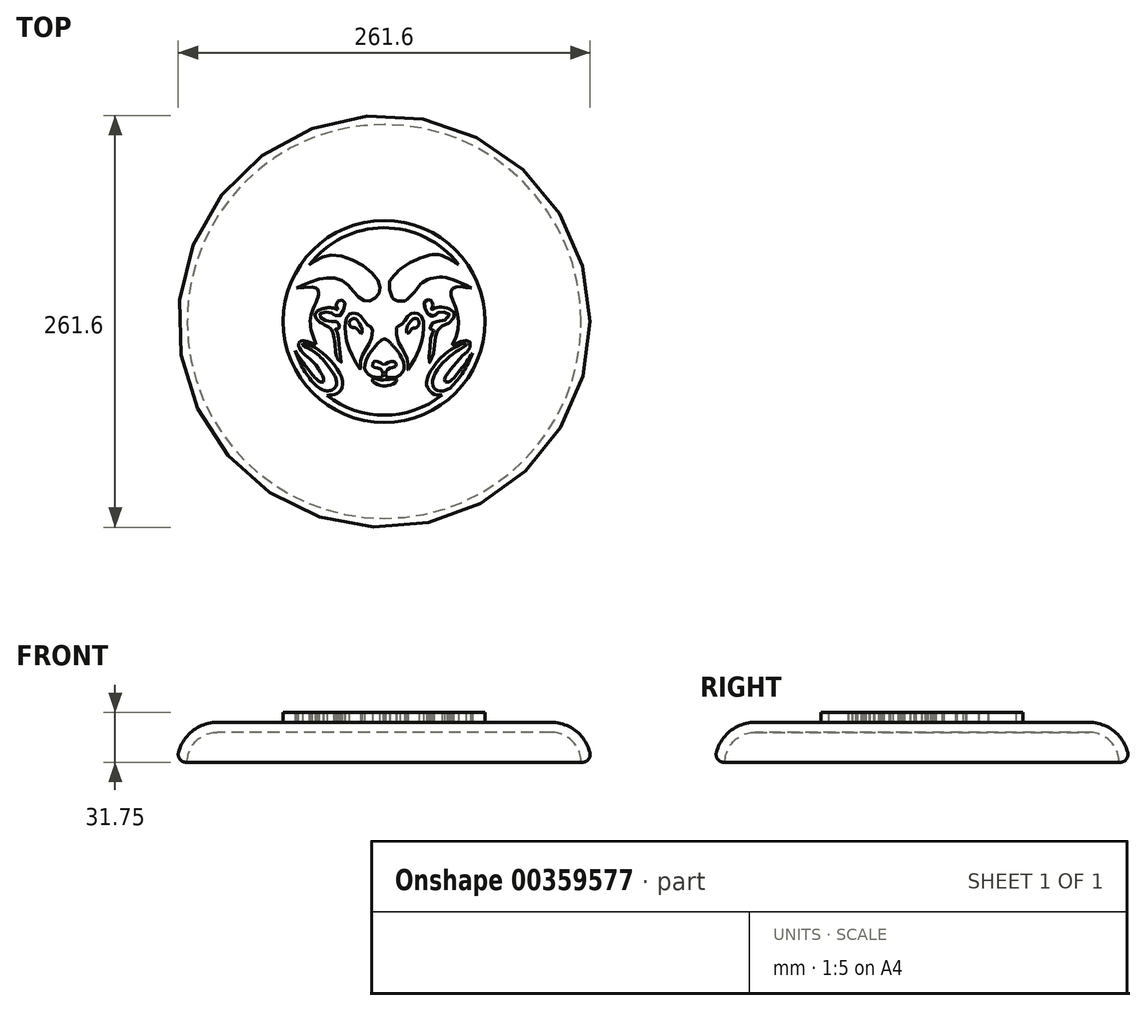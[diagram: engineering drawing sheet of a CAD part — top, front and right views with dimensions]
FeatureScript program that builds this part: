
annotation { "Feature Type Name" : "Feature", "Feature Type Description" : "" }
export const myFeature = defineFeature(function(context is Context, id is Id, definition is map)
    precondition{}
    {
        {
            var Q0;
            Q0=qCreatedBy(makeId("Top.planeOp"),FACE);
            var sketch = newSketch(context, id + "F0", { "sketchPlane" : qUnion([Q0])});
            skCircle(sketch, "E0", {"center": v(0, 0) * mm, "radius": 131.44 * mm});
            skSolve(sketch);
        }
        {
            var Q0;
            Q0=makeQuery(id+"F0.imprint","IMPRINT",FACE,{"disambiguationData":[TD([[makeQuery(id+"F0.imprint","IMPRINT",EDGE,{"derivedFrom":sQuery(id+"F0.wireOp",EDGE,"E0")}),1.0]])]});
            extrude(context, id + "F1", {"entities" : qUnion([Q0]), "depth" : 25.4 * mm});
        }
        {
            var Q0;
            Q0=makeQuery(id+"F1.opExtrude","CAP_EDGE",EDGE,{"disambiguationData":[OSD([sQuery(id+"F0.wireOp",EDGE,"E0")])],"isStart":false});
            fillet(context, id + "F2", {"entities" : qUnion([Q0]), "radius" : 25.4 * mm, "tangentPropagation" : true, "allowEdgeOverflow" : false});
        }
        {
            var Q0;
            {var subQ0=sQuery(id+"F0.wireOp",EDGE,"E0");Q0=makeQuery(id+"F2.opFillet","BLEND_EDGE",EDGE,{"blendedFrom":[makeQuery(id+"F1.opExtrude","CAP_EDGE",EDGE,{"disambiguationData":[OSD([subQ0])],"isStart":false}),makeQuery(id+"F1.opExtrude","CAP_FACE",FACE,{"disambiguationData":[OSD([subQ0])],"isStart":true})],"blendedInto":[makeQuery(id+"F1.opExtrude","CAP_FACE",FACE,{"disambiguationData":[OSD([subQ0])],"isStart":true})]});}
            fillet(context, id + "F3", {"entities" : qUnion([Q0]), "radius" : 5.08 * mm, "tangentPropagation" : true, "allowEdgeOverflow" : false});
        }
        {
            var Q0;
            Q0=makeQuery(id+"F1.opExtrude","CAP_FACE",FACE,{"disambiguationData":[OSD([sQuery(id+"F0.wireOp",EDGE,"E0")])],"isStart":true});
            shell(context, id + "F4", {"entities" : qUnion([Q0]), "thickness" : 6.35 * mm});
        }
        {
            var Q0;
            Q0=makeQuery(id+"F1.opExtrude","CAP_FACE",FACE,{"disambiguationData":[OSD([sQuery(id+"F0.wireOp",EDGE,"E0")])],"isStart":false});
            var sketch = newSketch(context, id + "F5", { "sketchPlane" : qUnion([Q0])});
            skCircle(sketch, "E1", {"center": v(0, 0) * mm, "radius": 67.22 * mm});
            skCircle(sketch, "E2", {"center": v(0, 0) * mm, "radius": 64.1 * mm});
            skCircle(sketch, "E3", {"center": v(0, 0) * mm, "radius": 59.52 * mm});
            skFitSpline(sketch, "E4", {"points": [v(-47.61, 35.71) * mm, v(-30.33, 42.03) * mm, v(-3.45, 25.44) * mm, v(-5.16, 15.48) * mm, v(-13.42, 13.42) * mm, v(-24.24, 24.18) * mm, v(-39.23, 27.35) * mm, v(-55.63, 21.17) * mm], "startDerivative": vector(77.27, 62.1) * mm, "endDerivative": vector(-80.83, -38.7) * mm});
            skFitSpline(sketch, "E5", {"points": [v(3.63, 26.05) * mm, v(11.7, 34.34) * mm, v(24.03, 40.71) * mm, v(34.24, 42.41) * mm, v(47.28, 36.15) * mm], "startDerivative": vector(32.1, 37.54) * mm, "endDerivative": vector(50.12, -31.58) * mm});
            skFitSpline(sketch, "E6", {"points": [v(3.63, 26.05) * mm, v(5.75, 14.57) * mm, v(13.4, 12.87) * mm], "startDerivative": vector(-3.44, -18.37) * mm, "endDerivative": vector(17, 0) * mm});
            skFitSpline(sketch, "E7", {"points": [v(13.4, 12.87) * mm, v(19.78, 19.46) * mm, v(23.18, 23.7) * mm, v(29.77, 27.32) * mm, v(38.28, 27.96) * mm, v(55.55, 21.36) * mm], "startDerivative": vector(36.21, 34.6) * mm, "endDerivative": vector(89.25, -41.03) * mm});
            skFitSpline(sketch, "E8", {"points": [v(-45.68, 22) * mm, v(-55.63, 21.17) * mm], "startDerivative": vector(-9.94, -0.84) * mm, "endDerivative": vector(-9.94, -0.84) * mm});
            skFitSpline(sketch, "E9", {"points": [v(-43.13, -14.76) * mm, v(-46.53, -4.56) * mm, v(-46.1, 5.43) * mm, v(-41.86, 16.06) * mm, v(-42.28, 20.3) * mm, v(-45.68, 22) * mm], "startDerivative": vector(-17.3, 43.12) * mm, "endDerivative": vector(-28.36, 8.66) * mm});
            skFitSpline(sketch, "E10", {"points": [v(-43.13, -14.76) * mm, v(-49.94, -12.43) * mm, v(-52.91, -12.43) * mm, v(-54.4, -14.76) * mm, v(-52.06, -19.44) * mm, v(-45.68, -25.18) * mm, v(-38.67, -35.6) * mm, v(-38.46, -38.36) * mm], "startDerivative": vector(-45.49, 17.24) * mm, "endDerivative": vector(-2.99, -22.74) * mm});
            skFitSpline(sketch, "E11", {"points": [v(-38.46, -38.36) * mm, v(-40.58, -38.36) * mm, v(-56.56, -18.53) * mm], "startDerivative": vector(-8.24, -2.87) * mm, "endDerivative": vector(-31.36, 47.89) * mm});
            skFitSpline(sketch, "E12", {"points": [v(-51.85, -14.13) * mm, v(-49.94, -14.34) * mm, v(-40.58, -18.8) * mm, v(-27.4, -34.53) * mm, v(-27.2, -43.03) * mm, v(-31.44, -46.22) * mm, v(-36.4, -47.09) * mm], "startDerivative": vector(19.14, -0.5) * mm, "endDerivative": vector(-34.7, -8.03) * mm});
            skFitSpline(sketch, "E13", {"points": [v(-51.85, -14.13) * mm, v(-51.85, -15.01) * mm, v(-48.61, -16.9) * mm, v(-39.08, -24) * mm, v(-32.25, -33) * mm], "startDerivative": vector(-2, -8.15) * mm, "endDerivative": vector(8.92, -10.28) * mm});
            skFitSpline(sketch, "E14", {"points": [v(-32.25, -33) * mm, v(-31.02, -35.52) * mm, v(-30.42, -37.85) * mm, v(-30.43, -40.22) * mm, v(-31.46, -42.3) * mm, v(-33.64, -43.63) * mm, v(-36, -44.03) * mm, v(-38.43, -43.74) * mm, v(-43.04, -41.1) * mm], "startDerivative": vector(10.86, -20.07) * mm, "endDerivative": vector(-28.3, 19.1) * mm});
            skFitSpline(sketch, "E15", {"points": [v(-29.55, 7.8) * mm, v(-30.23, 9.26) * mm, v(-30.4, 11.4) * mm, v(-29.55, 12.85) * mm, v(-28.18, 13.54) * mm, v(-26.64, 13.46) * mm, v(-25.27, 12.7) * mm, v(-24.84, 10.64) * mm, v(-26.64, 5.58) * mm, v(-28.27, 3.53) * mm, v(-30.75, 3.6) * mm, v(-32.25, 4.63) * mm, v(-33.64, 5.48) * mm, v(-36.57, 5.99) * mm, v(-40.33, 5.3) * mm, v(-40.85, 4.44) * mm, v(-40.76, 3.07) * mm, v(-38.7, 1.36) * mm, v(-35.63, 0) * mm, v(-32.25, 0) * mm, v(-30.58, 0) * mm, v(-29.13, -1.36) * mm, v(-28.36, -2.38) * mm, v(-28.27, -3.92) * mm, v(-29.56, -4.53) * mm, v(-30.58, -4.53) * mm, v(-31.01, -4.96) * mm, v(-30.41, -6.15) * mm, v(-29.3, -8.46) * mm, v(-28.88, -11.63) * mm, v(-28.8, -14.71) * mm, v(-27.68, -21.81) * mm, v(-27.52, -26.18) * mm, v(-29.23, -24.13) * mm], "startDerivative": vector(-29.16, 51.27) * mm, "endDerivative": vector(-36.35, 67.29) * mm});
            skFitSpline(sketch, "E16", {"points": [v(-29.23, -24.13) * mm, v(-30.17, -22.25) * mm, v(-30.93, -18.48) * mm, v(-31.44, -12.66) * mm, v(-32.47, -7.7) * mm, v(-33.66, -4.88) * mm, v(-35.46, -3.43) * mm, v(-38.97, -1.55) * mm, v(-42.73, 1.35) * mm, v(-43.93, 3.92) * mm], "startDerivative": vector(-11.7, 19.95) * mm, "endDerivative": vector(-4.1, 19.55) * mm});
            skFitSpline(sketch, "E17", {"points": [v(-43.93, 3.92) * mm, v(-43.73, 4.9) * mm, v(-42.95, 6.2) * mm, v(-41.25, 7.23) * mm, v(-38.61, 8.17) * mm, v(-36.68, 8.64) * mm, v(-33.58, 8.75) * mm, v(-30.87, 7.92) * mm, v(-29.8, 7.41) * mm, v(-29.55, 7.8) * mm], "startDerivative": vector(1.43, 11.35) * mm, "endDerivative": vector(3.04, 9.31) * mm});
            skFitSpline(sketch, "E18", {"points": [v(-19.48, 5.43) * mm, v(-22.36, 4.44) * mm, v(-24.06, 1.7) * mm, v(-24.65, -0.96) * mm, v(-24.8, -6.22) * mm, v(-22.96, -15.3) * mm, v(-19.2, -23.73) * mm, v(-14.92, -30.38) * mm, v(-14.99, -28.3) * mm, v(-14.25, -22.54) * mm, v(-10.77, -16.24) * mm, v(-8.33, -11.28) * mm, v(-7.58, -4.1) * mm, v(-8.91, -3.37) * mm, v(-12.02, -0.71) * mm, v(-14.38, 2.68) * mm, v(-16.08, 4.44) * mm, v(-19.48, 5.43) * mm]});
            skFitSpline(sketch, "E19", {"points": [v(-14.75, -7.52) * mm, v(-14.16, -7.3) * mm, v(-14.38, -4.2) * mm, v(-16.52, 0) * mm, v(-18.22, 1.56) * mm, v(-20, 1.7) * mm, v(-21.18, 1.04) * mm, v(-22, 0) * mm, v(-21.85, -2.59) * mm, v(-20.07, -3.84) * mm, v(-18.6, -3.9) * mm, v(-16.9, -4.8) * mm, v(-14.75, -7.52) * mm]});
            skFitSpline(sketch, "E20", {"points": [v(7.72, -3.92) * mm, v(8.6, -3.33) * mm, v(10, -2.59) * mm, v(12.08, -0.96) * mm, v(14.15, 2.16) * mm, v(16.15, 4.44) * mm, v(18.14, 5.43) * mm, v(19.77, 5.43) * mm, v(22.58, 4.44) * mm, v(24.5, 1.44) * mm, v(25.08, -3.51) * mm, v(24.2, -11.43) * mm, v(21.16, -20.16) * mm, v(15.24, -30.53) * mm, v(15.1, -30.68) * mm, v(15.1, -27.72) * mm, v(14.13, -22.62) * mm, v(11.4, -17.08) * mm, v(8.75, -12.28) * mm, v(7.72, -3.92) * mm]});
            skFitSpline(sketch, "E21", {"points": [v(14.51, -7.3) * mm, v(14.3, -5.83) * mm, v(14.66, -3.02) * mm, v(16.59, 0) * mm, v(18.36, 1.5) * mm, v(19.62, 1.87) * mm, v(20.8, 1.8) * mm, v(21.98, 0) * mm, v(21.98, -2.41) * mm, v(19.98, -4.04) * mm, v(18.58, -4.12) * mm, v(16.8, -5.45) * mm, v(15.7, -7.3) * mm, v(14.51, -7.3) * mm]});
            skFitSpline(sketch, "E22", {"points": [v(0, -11.29) * mm, v(-1.32, -11.66) * mm, v(-6.18, -16.4) * mm, v(-10.78, -22.9) * mm, v(-12.53, -28.75) * mm, v(-11.9, -31.23) * mm, v(-9.92, -33.6) * mm, v(-6.93, -35.2) * mm, v(-1.33, -35.2) * mm, v(-0.59, -33.44) * mm, v(-1.02, -31.72) * mm, v(-2.43, -30.37) * mm, v(-4.18, -29.58) * mm, v(-6.33, -29.15) * mm, v(-7.25, -28.58) * mm, v(-7.3, -26.82) * mm, v(-6.46, -25.41) * mm, v(-4.93, -25.2) * mm, v(-2.47, -25.98) * mm, v(0, -27.64) * mm], "startDerivative": vector(-31.8, -2.62) * mm, "endDerivative": vector(44.21, -33.7) * mm});
            skFitSpline(sketch, "E23", {"points": [v(0, -27.64) * mm, v(0.87, -27.03) * mm, v(2.45, -26.05) * mm, v(5.3, -25.39) * mm, v(6.8, -25.6) * mm, v(7.54, -27.03) * mm, v(7.5, -28.28) * mm, v(5.38, -29.25) * mm, v(3.5, -29.7) * mm, v(1.56, -31.24) * mm, v(0.95, -33.08) * mm, v(1.08, -34.75) * mm, v(2.92, -35.5) * mm, v(7.44, -35.22) * mm, v(11.48, -32.66) * mm, v(12.76, -29.15) * mm, v(12.01, -25.37) * mm, v(10, -21.16) * mm, v(10, -21.3) * mm], "startDerivative": vector(21.67, 14.87) * mm, "endDerivative": vector(2.26, -14.92) * mm});
            skFitSpline(sketch, "E24", {"points": [v(10, -21.16) * mm, v(7.98, -18.18) * mm, v(4.89, -14.7) * mm, v(2.57, -12.26) * mm, v(0, -11.29) * mm], "startDerivative": vector(-7.23, 11.72) * mm, "endDerivative": vector(-17.66, -0.8) * mm});
            skFitSpline(sketch, "E25", {"points": [v(-6.79, -36.27) * mm, v(-3.38, -36.84) * mm, v(0, -37.08) * mm, v(4.64, -36.65) * mm, v(7.17, -36.5) * mm, v(7.9, -36.77) * mm, v(7.22, -38.66) * mm, v(3.23, -40.45) * mm, v(0.5, -40.93) * mm, v(-3.38, -40.26) * mm, v(-6.63, -38.74) * mm, v(-7.31, -37.9) * mm, v(-7.36, -36.85) * mm, v(-6.79, -36.27) * mm]});
            skFitSpline(sketch, "E26", {"points": [v(55.55, 21.36) * mm, v(51.55, 21.66) * mm, v(48.5, 22.07) * mm, v(45.1, 21.86) * mm, v(43.46, 20.87) * mm, v(42.63, 19.97) * mm, v(42.27, 18.36) * mm, v(42.6, 15.67) * mm, v(44.35, 11.35) * mm, v(46.54, 4.83) * mm, v(47.07, -2.33) * mm, v(45.4, -10.18) * mm, v(43.14, -15.31) * mm, v(46.3, -13.8) * mm, v(51.13, -12.13) * mm, v(54, -12.5) * mm, v(54.9, -15.06) * mm, v(52.88, -19.1) * mm, v(50.62, -20.95) * mm, v(43.1, -29.12) * mm, v(39.85, -33.64) * mm], "startDerivative": vector(-84.35, 4.69) * mm, "endDerivative": vector(-30.59, -53.96) * mm});
            skFitSpline(sketch, "E27", {"points": [v(39.85, -33.64) * mm, v(38.77, -35.63) * mm, v(38.67, -38.25) * mm, v(41.39, -38.16) * mm, v(46.09, -33.64) * mm, v(51.06, -27.2) * mm, v(56.04, -20.04) * mm], "startDerivative": vector(-10.25, -15.17) * mm, "endDerivative": vector(21.92, 32.35) * mm});
            skFitSpline(sketch, "E28", {"points": [v(52.03, -14.06) * mm, v(51.3, -13.85) * mm, v(46.08, -15.9) * mm, v(41.17, -18.63) * mm, v(33.17, -26.27) * mm, v(27.84, -34.54) * mm, v(27.08, -37.4) * mm, v(26.93, -39.63) * mm, v(28.02, -42.86) * mm, v(31.5, -45.99) * mm, v(34.03, -46.78) * mm, v(36.82, -46.76) * mm], "startDerivative": vector(-14.14, 9.02) * mm, "endDerivative": vector(38.58, 2.68) * mm});
            skFitSpline(sketch, "E29", {"points": [v(52.03, -14.06) * mm, v(52.33, -14.5) * mm, v(51.77, -15.32) * mm, v(48, -17.66) * mm, v(44.02, -20.3) * mm, v(39.01, -24.61) * mm, v(33.93, -30.48) * mm, v(30.95, -36.6) * mm, v(30.75, -39.3) * mm, v(31.5, -41.59) * mm, v(32.33, -42.86) * mm, v(33.85, -43.92) * mm, v(37.33, -44.24) * mm, v(42.03, -42.14) * mm], "startDerivative": vector(14.03, -13.8) * mm, "endDerivative": vector(49.7, 28.64) * mm});
            skFitSpline(sketch, "E30", {"points": [v(28.02, 13.77) * mm, v(29.3, 13.5) * mm, v(30.47, 12.34) * mm, v(30.81, 11.02) * mm, v(30.85, 9.5) * mm, v(30.2, 8.53) * mm, v(29.98, 7.84) * mm, v(30.45, 7.7) * mm, v(32.15, 8.42) * mm, v(34.93, 9) * mm, v(38.75, 8.7) * mm, v(42.54, 7.19) * mm, v(44.16, 5.64) * mm, v(44.45, 4.16) * mm, v(44.05, 2.1) * mm], "startDerivative": vector(21.18, -1.44) * mm, "endDerivative": vector(-6.98, -27.5) * mm});
            skFitSpline(sketch, "E31", {"points": [v(44.05, 2.1) * mm, v(43.08, 0.92) * mm, v(40.68, -1.15) * mm, v(37.43, -2.68) * mm, v(35.72, -3.56) * mm, v(34.51, -4.73) * mm, v(33.21, -7.56) * mm, v(32.79, -9.04) * mm, v(32.45, -10.35) * mm, v(31.9, -15.86) * mm, v(31.64, -19.16) * mm, v(29.7, -24.74) * mm, v(28.45, -26.26) * mm, v(28.32, -22.67) * mm, v(28.9, -20.57) * mm, v(29.3, -15.27) * mm, v(29.46, -10.55) * mm, v(30.65, -6.7) * mm, v(31.82, -4.8) * mm, v(29.39, -4.75) * mm, v(28.9, -2.99) * mm, v(30.43, -1.02) * mm, v(31.24, -0.43) * mm, v(32.34, 0) * mm, v(35.75, 0.19) * mm, v(38.93, 1.16) * mm, v(41.39, 3.39) * mm, v(41.25, 4.76) * mm, v(39.8, 5.54) * mm, v(37.48, 5.94) * mm, v(35.48, 5.95) * mm, v(34.04, 5.42) * mm, v(32.17, 3.88) * mm, v(30.83, 3.32) * mm, v(28.65, 3.9) * mm, v(27.04, 6) * mm, v(26.26, 7.6) * mm, v(25.69, 9.27) * mm, v(25.43, 10.94) * mm, v(25.69, 12.42) * mm, v(26.52, 13.31) * mm, v(28.02, 13.77) * mm], "startDerivative": vector(-43.21, -56.66) * mm, "endDerivative": vector(81.46, 17.12) * mm});
            skSolve(sketch);
        }
        {
            var Q0;
            {var subQ0=sQuery(id+"F5.wireOp",EDGE,"E4");Q0=makeQuery(id+"F5.imprint","IMPRINT",FACE,{"disambiguationData":[TD([[makeQuery(id+"F5.imprint","IMPRINT",EDGE,{"derivedFrom":subQ0}),-1.0]])]});}
            var Q1;
            {var subQ0=sQuery(id+"F5.wireOp",EDGE,"E5");Q1=makeQuery(id+"F5.imprint","IMPRINT",FACE,{"disambiguationData":[TD([[makeQuery(id+"F5.imprint","IMPRINT",EDGE,{"derivedFrom":subQ0}),-1.0]])]});}
            var Q2;
            Q2=makeQuery(id+"F5.imprint","IMPRINT",FACE,{"disambiguationData":[TD([[makeQuery(id+"F5.imprint","IMPRINT",EDGE,{"derivedFrom":sQuery(id+"F5.wireOp",EDGE,"E30")}),-1.0]])]});
            var Q3;
            Q3=makeQuery(id+"F5.imprint","IMPRINT",FACE,{"disambiguationData":[TD([[makeQuery(id+"F5.imprint","IMPRINT",EDGE,{"derivedFrom":sQuery(id+"F5.wireOp",EDGE,"E20")}),-1.0]])]});
            var Q4;
            Q4=makeQuery(id+"F5.imprint","IMPRINT",FACE,{"disambiguationData":[TD([[makeQuery(id+"F5.imprint","IMPRINT",EDGE,{"derivedFrom":sQuery(id+"F5.wireOp",EDGE,"E18")}),1.0]])]});
            var Q5;
            {var subQ0=sQuery(id+"F5.wireOp",EDGE,"E22");Q5=makeQuery(id+"F5.imprint","IMPRINT",FACE,{"disambiguationData":[TD([[makeQuery(id+"F5.imprint","IMPRINT",EDGE,{"derivedFrom":subQ0}),1.0]])]});}
            var Q6;
            Q6=makeQuery(id+"F5.imprint","IMPRINT",FACE,{"disambiguationData":[TD([[makeQuery(id+"F5.imprint","IMPRINT",EDGE,{"derivedFrom":sQuery(id+"F5.wireOp",EDGE,"E25")}),-1.0]])]});
            var Q7;
            {var subQ0=sQuery(id+"F5.wireOp",EDGE,"E28");Q7=makeQuery(id+"F5.imprint","IMPRINT",FACE,{"disambiguationData":[TD([[makeQuery(id+"F5.imprint","IMPRINT",EDGE,{"derivedFrom":subQ0}),1.0]])]});}
            var Q8;
            {var subQ0=sQuery(id+"F5.wireOp",EDGE,"E26");Q8=makeQuery(id+"F5.imprint","IMPRINT",FACE,{"disambiguationData":[TD([[makeQuery(id+"F5.imprint","IMPRINT",EDGE,{"derivedFrom":subQ0}),1.0]])]});}
            var Q9;
            {var subQ0=sQuery(id+"F5.wireOp",EDGE,"E8");Q9=makeQuery(id+"F5.imprint","IMPRINT",FACE,{"disambiguationData":[TD([[makeQuery(id+"F5.imprint","IMPRINT",EDGE,{"derivedFrom":subQ0}),1.0]])]});}
            var Q10;
            {var subQ0=sQuery(id+"F5.wireOp",EDGE,"E12");Q10=makeQuery(id+"F5.imprint","IMPRINT",FACE,{"disambiguationData":[TD([[makeQuery(id+"F5.imprint","IMPRINT",EDGE,{"derivedFrom":subQ0}),-1.0]])]});}
            var Q11;
            Q11=makeQuery(id+"F5.imprint","IMPRINT",FACE,{"disambiguationData":[TD([[makeQuery(id+"F5.imprint","IMPRINT",EDGE,{"derivedFrom":sQuery(id+"F5.wireOp",EDGE,"E15")}),-1.0]])]});
            var Q12;
            Q12=makeQuery(id+"F5.imprint","IMPRINT",FACE,{"disambiguationData":[TD([[makeQuery(id+"F5.imprint","IMPRINT",EDGE,{"derivedFrom":sQuery(id+"F5.wireOp",EDGE,"E2")}),1.0]])]});
            extrude(context, id + "F6", {"entities" : qUnion([Q0, Q1, Q2, Q3, Q4, Q5, Q6, Q7, Q8, Q9, Q10, Q11, Q12]), "operationType" : NewBodyOperationType.ADD, "depth" : 6.35 * mm});
        }
    });
